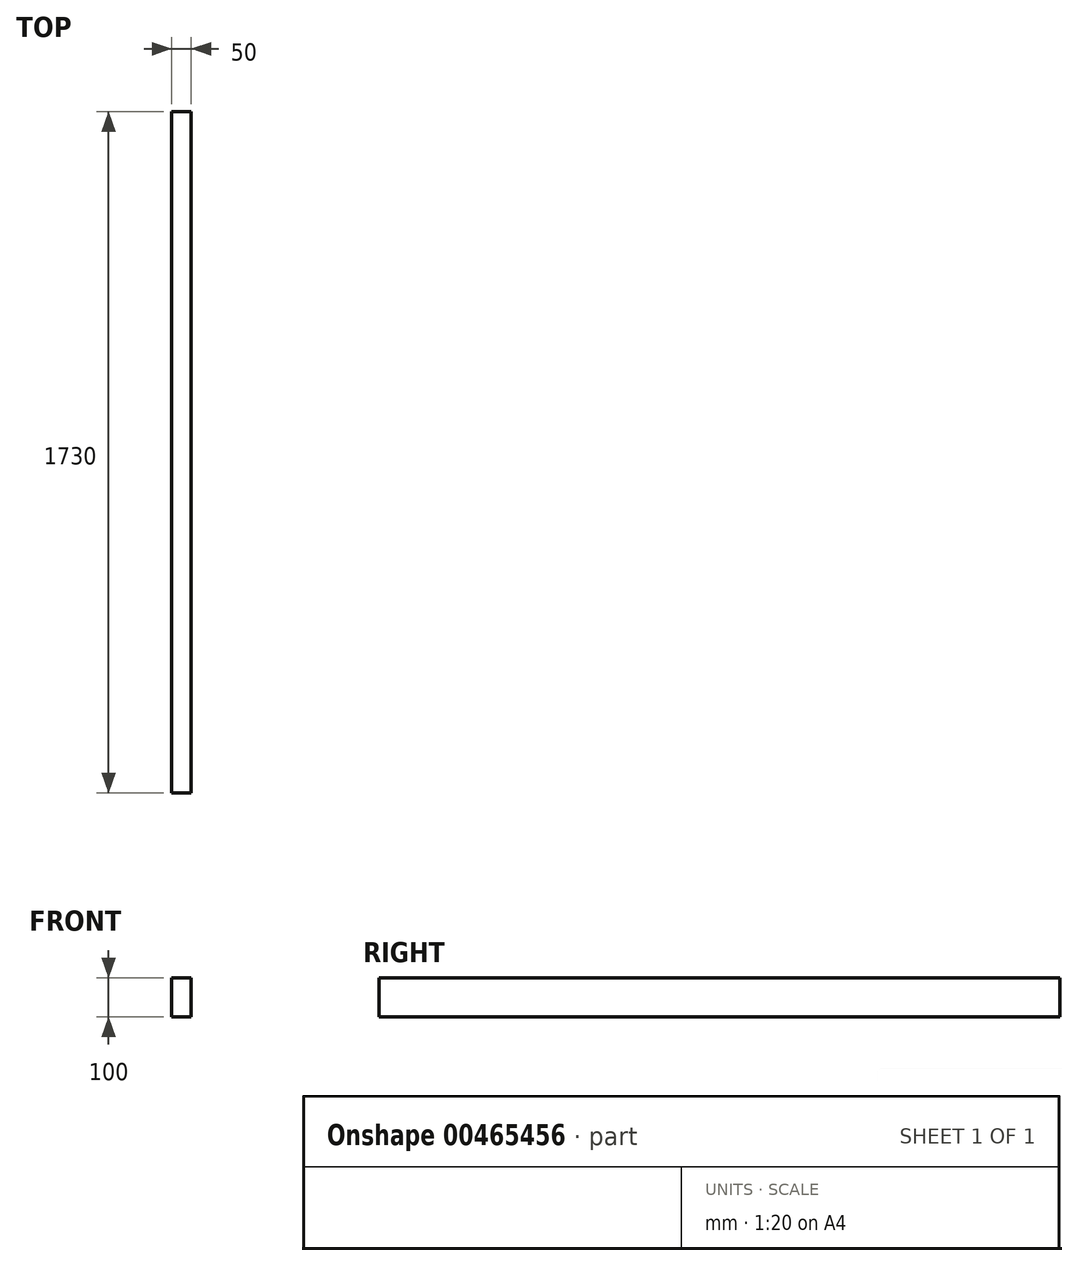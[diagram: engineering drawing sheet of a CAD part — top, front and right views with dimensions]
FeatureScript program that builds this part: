
annotation { "Feature Type Name" : "Feature", "Feature Type Description" : "" }
export const myFeature = defineFeature(function(context is Context, id is Id, definition is map)
    precondition{}
    {
        {
            var Q0;
            Q0=qCreatedBy(makeId("Front.planeOp"),FACE);
            var sketch = newSketch(context, id + "F0", { "sketchPlane" : qUnion([Q0])});
            skLineSegment(sketch, "E0.bottom", {"start": v(31.76, 21.1) * mm, "end": v(81.76, 21.1) * mm});
            skLineSegment(sketch, "E0.top", {"start": v(31.76, 121.1) * mm, "end": v(81.76, 121.1) * mm});
            skLineSegment(sketch, "E0.left", {"start": v(31.76, 21.1) * mm, "end": v(31.76, 121.1) * mm});
            skLineSegment(sketch, "E0.right", {"start": v(81.76, 21.1) * mm, "end": v(81.76, 121.1) * mm});
            skSolve(sketch);
        }
        {
            var Q0;
            Q0=qSketchRegion(id+"F0",true);
            extrude(context, id + "F1", {"entities" : qUnion([Q0]), "oppositeDirection" : true, "depth" : 1730 * mm});
        }
    });
